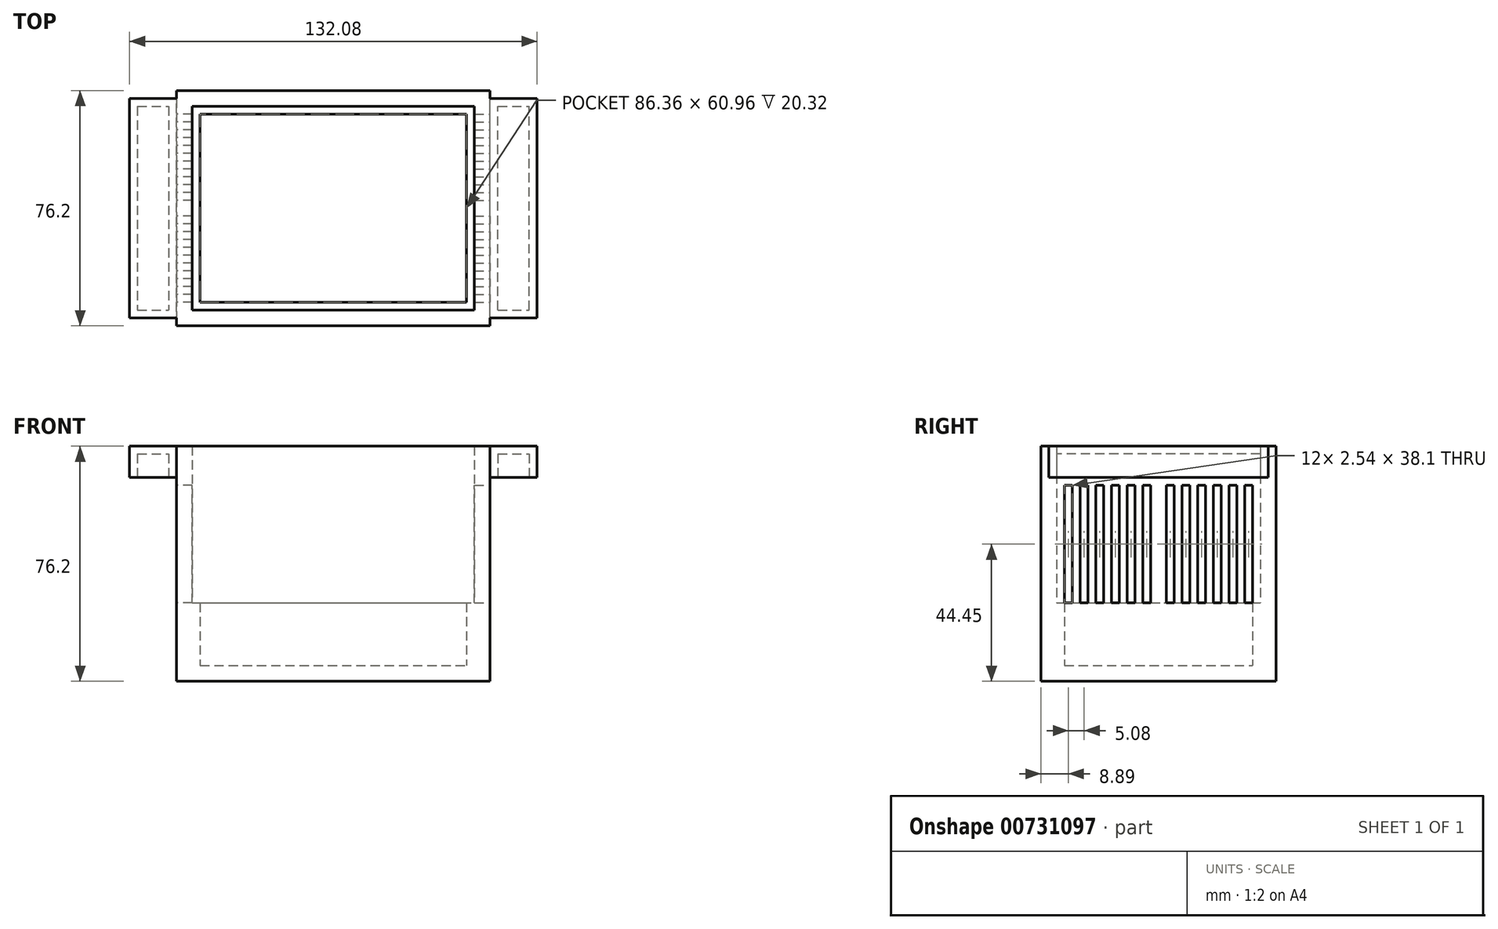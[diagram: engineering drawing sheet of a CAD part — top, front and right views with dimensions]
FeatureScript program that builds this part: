
annotation { "Feature Type Name" : "Feature", "Feature Type Description" : "" }
export const myFeature = defineFeature(function(context is Context, id is Id, definition is map)
    precondition{}
    {
        {
            var Q0;
            Q0=qCreatedBy(makeId("Top.planeOp"),FACE);
            var sketch = newSketch(context, id + "F0", { "sketchPlane" : qUnion([Q0])});
            skLineSegment(sketch, "E0.bottom", {"start": v(-50.8, -38.1) * mm, "end": v(50.8, -38.1) * mm});
            skLineSegment(sketch, "E0.top", {"start": v(-50.8, 38.1) * mm, "end": v(50.8, 38.1) * mm});
            skLineSegment(sketch, "E0.left", {"start": v(-50.8, -38.1) * mm, "end": v(-50.8, 38.1) * mm});
            skLineSegment(sketch, "E0.right", {"start": v(50.8, -38.1) * mm, "end": v(50.8, 38.1) * mm});
            skLineSegment(sketch, "E1.bottom", {"start": v(-45.72, -33.02) * mm, "end": v(45.72, -33.02) * mm});
            skLineSegment(sketch, "E1.top", {"start": v(-45.72, 33.02) * mm, "end": v(45.72, 33.02) * mm});
            skLineSegment(sketch, "E1.left", {"start": v(-45.72, -33.02) * mm, "end": v(-45.72, 33.02) * mm});
            skLineSegment(sketch, "E1.right", {"start": v(45.72, -33.02) * mm, "end": v(45.72, 33.02) * mm});
            skLineSegment(sketch, "E2.bottom", {"start": v(-43.18, -30.48) * mm, "end": v(43.18, -30.48) * mm});
            skLineSegment(sketch, "E2.top", {"start": v(-43.18, 30.48) * mm, "end": v(43.18, 30.48) * mm});
            skLineSegment(sketch, "E2.left", {"start": v(-43.18, -30.48) * mm, "end": v(-43.18, 30.48) * mm});
            skLineSegment(sketch, "E2.right", {"start": v(43.18, -30.48) * mm, "end": v(43.18, 30.48) * mm});
            skSolve(sketch);
        }
        {
            var Q0;
            Q0=makeQuery(id+"F0.imprint","IMPRINT",FACE,{"disambiguationData":[TD([[makeQuery(id+"F0.imprint","IMPRINT",EDGE,{"derivedFrom":sQuery(id+"F0.wireOp",EDGE,"E1.bottom")}),1.0]])]});
            extrude(context, id + "F1", {"entities" : qUnion([Q0]), "depth" : 25.4 * mm, "offsetDistance" : 25.4 * mm});
        }
        {
            var Q0;
            Q0 = qSketchRegion(id + "F0", true);
            extrude(context, id + "F2", {"entities" : qUnion([Q0]), "operationType" : NewBodyOperationType.ADD, "depth" : 76.2 * mm, "offsetDistance" : 25.4 * mm});
        }
        {
            var Q0;
            Q0=makeQuery(id+"F2.opExtrude","SWEPT_FACE",FACE,{"disambiguationData":[OSD([sQuery(id+"F0.wireOp",EDGE,"E0.left")])]});
            var sketch = newSketch(context, id + "F3", { "sketchPlane" : qUnion([Q0])});
            skLineSegment(sketch, "E3.bottom", {"start": v(-30.48, 25.4) * mm, "end": v(-27.94, 25.4) * mm});
            skLineSegment(sketch, "E3.top", {"start": v(-30.48, 63.5) * mm, "end": v(-27.94, 63.5) * mm});
            skLineSegment(sketch, "E3.left", {"start": v(-30.48, 25.4) * mm, "end": v(-30.48, 63.5) * mm});
            skLineSegment(sketch, "E3.right", {"start": v(-27.94, 25.4) * mm, "end": v(-27.94, 63.5) * mm});
            skLineSegment(sketch, "E4.bottom", {"start": v(-25.4, 25.4) * mm, "end": v(-22.86, 25.4) * mm});
            skLineSegment(sketch, "E4.top", {"start": v(-25.4, 63.5) * mm, "end": v(-22.86, 63.5) * mm});
            skLineSegment(sketch, "E4.left", {"start": v(-25.4, 25.4) * mm, "end": v(-25.4, 63.5) * mm});
            skLineSegment(sketch, "E4.right", {"start": v(-22.86, 25.4) * mm, "end": v(-22.86, 63.5) * mm});
            skLineSegment(sketch, "E5.bottom", {"start": v(-20.32, 25.4) * mm, "end": v(-17.78, 25.4) * mm});
            skLineSegment(sketch, "E5.top", {"start": v(-20.32, 63.5) * mm, "end": v(-17.78, 63.5) * mm});
            skLineSegment(sketch, "E5.left", {"start": v(-20.32, 25.4) * mm, "end": v(-20.32, 63.5) * mm});
            skLineSegment(sketch, "E5.right", {"start": v(-17.78, 25.4) * mm, "end": v(-17.78, 63.5) * mm});
            skLineSegment(sketch, "E6.bottom", {"start": v(-15.24, 25.4) * mm, "end": v(-12.7, 25.4) * mm});
            skLineSegment(sketch, "E6.top", {"start": v(-15.24, 63.5) * mm, "end": v(-12.7, 63.5) * mm});
            skLineSegment(sketch, "E6.left", {"start": v(-12.7, 25.4) * mm, "end": v(-12.7, 63.5) * mm});
            skLineSegment(sketch, "E6.right", {"start": v(-15.24, 25.4) * mm, "end": v(-15.24, 63.5) * mm});
            skLineSegment(sketch, "E7.bottom", {"start": v(-10.16, 25.4) * mm, "end": v(-7.62, 25.4) * mm});
            skLineSegment(sketch, "E7.top", {"start": v(-10.16, 63.5) * mm, "end": v(-7.62, 63.5) * mm});
            skLineSegment(sketch, "E7.left", {"start": v(-10.16, 25.4) * mm, "end": v(-10.16, 63.5) * mm});
            skLineSegment(sketch, "E7.right", {"start": v(-7.62, 25.4) * mm, "end": v(-7.62, 63.5) * mm});
            skLineSegment(sketch, "E8.bottom", {"start": v(-5.08, 25.4) * mm, "end": v(-2.54, 25.4) * mm});
            skLineSegment(sketch, "E8.top", {"start": v(-5.08, 63.5) * mm, "end": v(-2.54, 63.5) * mm});
            skLineSegment(sketch, "E8.left", {"start": v(-5.08, 25.4) * mm, "end": v(-5.08, 63.5) * mm});
            skLineSegment(sketch, "E8.right", {"start": v(-2.54, 25.4) * mm, "end": v(-2.54, 63.5) * mm});
            skLineSegment(sketch, "E9.bottom", {"start": v(2.54, 25.4) * mm, "end": v(5.08, 25.4) * mm});
            skLineSegment(sketch, "E9.top", {"start": v(2.54, 63.5) * mm, "end": v(5.08, 63.5) * mm});
            skLineSegment(sketch, "E9.left", {"start": v(2.54, 25.4) * mm, "end": v(2.54, 63.5) * mm});
            skLineSegment(sketch, "E9.right", {"start": v(5.08, 25.4) * mm, "end": v(5.08, 63.5) * mm});
            skLineSegment(sketch, "E10.bottom", {"start": v(7.62, 25.4) * mm, "end": v(10.16, 25.4) * mm});
            skLineSegment(sketch, "E10.top", {"start": v(7.62, 63.5) * mm, "end": v(10.16, 63.5) * mm});
            skLineSegment(sketch, "E10.left", {"start": v(7.62, 25.4) * mm, "end": v(7.62, 63.5) * mm});
            skLineSegment(sketch, "E10.right", {"start": v(10.16, 25.4) * mm, "end": v(10.16, 63.5) * mm});
            skLineSegment(sketch, "E11.bottom", {"start": v(12.7, 25.4) * mm, "end": v(15.24, 25.4) * mm});
            skLineSegment(sketch, "E11.top", {"start": v(12.7, 63.5) * mm, "end": v(15.24, 63.5) * mm});
            skLineSegment(sketch, "E11.left", {"start": v(12.7, 25.4) * mm, "end": v(12.7, 63.5) * mm});
            skLineSegment(sketch, "E11.right", {"start": v(15.24, 25.4) * mm, "end": v(15.24, 63.5) * mm});
            skLineSegment(sketch, "E12.bottom", {"start": v(17.78, 25.4) * mm, "end": v(20.32, 25.4) * mm});
            skLineSegment(sketch, "E12.top", {"start": v(17.78, 63.5) * mm, "end": v(20.32, 63.5) * mm});
            skLineSegment(sketch, "E12.left", {"start": v(17.78, 25.4) * mm, "end": v(17.78, 63.5) * mm});
            skLineSegment(sketch, "E12.right", {"start": v(20.32, 25.4) * mm, "end": v(20.32, 63.5) * mm});
            skLineSegment(sketch, "E13.bottom", {"start": v(22.86, 25.4) * mm, "end": v(25.4, 25.4) * mm});
            skLineSegment(sketch, "E13.top", {"start": v(22.86, 63.5) * mm, "end": v(25.4, 63.5) * mm});
            skLineSegment(sketch, "E13.left", {"start": v(22.86, 25.4) * mm, "end": v(22.86, 63.5) * mm});
            skLineSegment(sketch, "E13.right", {"start": v(25.4, 25.4) * mm, "end": v(25.4, 63.5) * mm});
            skLineSegment(sketch, "E14.bottom", {"start": v(27.94, 25.4) * mm, "end": v(30.48, 25.4) * mm});
            skLineSegment(sketch, "E14.top", {"start": v(27.94, 63.5) * mm, "end": v(30.48, 63.5) * mm});
            skLineSegment(sketch, "E14.left", {"start": v(27.94, 25.4) * mm, "end": v(27.94, 63.5) * mm});
            skLineSegment(sketch, "E14.right", {"start": v(30.48, 25.4) * mm, "end": v(30.48, 63.5) * mm});
            skSolve(sketch);
        }
        {
            var Q0;
            Q0 = qSketchRegion(id + "F3", true);
            extrude(context, id + "F4", {"entities" : qUnion([Q0]), "operationType" : NewBodyOperationType.REMOVE, "oppositeDirection" : true, "depth" : 5.08 * mm, "offsetDistance" : 25.4 * mm});
        }
        {
            var Q0;
            Q0=makeQuery(id+"F0.imprint","IMPRINT",FACE,{"disambiguationData":[TD([[makeQuery(id+"F0.imprint","IMPRINT",EDGE,{"derivedFrom":sQuery(id+"F0.wireOp",EDGE,"E2.bottom")}),1.0]])]});
            extrude(context, id + "F5", {"entities" : qUnion([Q0]), "operationType" : NewBodyOperationType.ADD, "depth" : 5.08 * mm, "offsetDistance" : 25.4 * mm});
        }
        {
            var Q0;
            Q0=makeQuery(id+"F2.opExtrude","SWEPT_FACE",FACE,{"disambiguationData":[OSD([sQuery(id+"F0.wireOp",EDGE,"E0.right")])]});
            var sketch = newSketch(context, id + "F6", { "sketchPlane" : qUnion([Q0])});
            skLineSegment(sketch, "E15.bottom", {"start": v(-2.54, 25.4) * mm, "end": v(-5.08, 25.4) * mm});
            skLineSegment(sketch, "E15.top", {"start": v(-2.54, 63.5) * mm, "end": v(-5.08, 63.5) * mm});
            skLineSegment(sketch, "E15.left", {"start": v(-2.54, 25.4) * mm, "end": v(-2.54, 63.5) * mm});
            skLineSegment(sketch, "E15.right", {"start": v(-5.08, 25.4) * mm, "end": v(-5.08, 63.5) * mm});
            skLineSegment(sketch, "E16.bottom", {"start": v(2.54, 25.4) * mm, "end": v(5.08, 25.4) * mm});
            skLineSegment(sketch, "E16.top", {"start": v(2.54, 63.5) * mm, "end": v(5.08, 63.5) * mm});
            skLineSegment(sketch, "E16.left", {"start": v(2.54, 25.4) * mm, "end": v(2.54, 63.5) * mm});
            skLineSegment(sketch, "E16.right", {"start": v(5.08, 25.4) * mm, "end": v(5.08, 63.5) * mm});
            skLineSegment(sketch, "E17.bottom", {"start": v(7.62, 25.4) * mm, "end": v(10.16, 25.4) * mm});
            skLineSegment(sketch, "E17.top", {"start": v(7.62, 63.5) * mm, "end": v(10.16, 63.5) * mm});
            skLineSegment(sketch, "E17.left", {"start": v(7.62, 25.4) * mm, "end": v(7.62, 63.5) * mm});
            skLineSegment(sketch, "E17.right", {"start": v(10.16, 25.4) * mm, "end": v(10.16, 63.5) * mm});
            skLineSegment(sketch, "E18.bottom", {"start": v(12.7, 25.4) * mm, "end": v(15.24, 25.4) * mm});
            skLineSegment(sketch, "E18.top", {"start": v(12.7, 63.5) * mm, "end": v(15.24, 63.5) * mm});
            skLineSegment(sketch, "E18.left", {"start": v(12.7, 25.4) * mm, "end": v(12.7, 63.5) * mm});
            skLineSegment(sketch, "E18.right", {"start": v(15.24, 25.4) * mm, "end": v(15.24, 63.5) * mm});
            skLineSegment(sketch, "E19.bottom", {"start": v(-7.62, 25.4) * mm, "end": v(-10.16, 25.4) * mm});
            skLineSegment(sketch, "E19.top", {"start": v(-7.62, 63.5) * mm, "end": v(-10.16, 63.5) * mm});
            skLineSegment(sketch, "E19.left", {"start": v(-7.62, 25.4) * mm, "end": v(-7.62, 63.5) * mm});
            skLineSegment(sketch, "E19.right", {"start": v(-10.16, 25.4) * mm, "end": v(-10.16, 63.5) * mm});
            skLineSegment(sketch, "E20.bottom", {"start": v(-12.7, 25.4) * mm, "end": v(-15.24, 25.4) * mm});
            skLineSegment(sketch, "E20.top", {"start": v(-12.7, 63.5) * mm, "end": v(-15.24, 63.5) * mm});
            skLineSegment(sketch, "E20.left", {"start": v(-12.7, 25.4) * mm, "end": v(-12.7, 63.5) * mm});
            skLineSegment(sketch, "E20.right", {"start": v(-15.24, 25.4) * mm, "end": v(-15.24, 63.5) * mm});
            skLineSegment(sketch, "E21.bottom", {"start": v(17.78, 25.4) * mm, "end": v(20.32, 25.4) * mm});
            skLineSegment(sketch, "E21.top", {"start": v(17.78, 63.5) * mm, "end": v(20.32, 63.5) * mm});
            skLineSegment(sketch, "E21.left", {"start": v(17.78, 25.4) * mm, "end": v(17.78, 63.5) * mm});
            skLineSegment(sketch, "E21.right", {"start": v(20.32, 25.4) * mm, "end": v(20.32, 63.5) * mm});
            skLineSegment(sketch, "E22.bottom", {"start": v(22.86, 25.4) * mm, "end": v(25.4, 25.4) * mm});
            skLineSegment(sketch, "E22.top", {"start": v(22.86, 63.5) * mm, "end": v(25.4, 63.5) * mm});
            skLineSegment(sketch, "E22.left", {"start": v(22.86, 25.4) * mm, "end": v(22.86, 63.5) * mm});
            skLineSegment(sketch, "E22.right", {"start": v(25.4, 25.4) * mm, "end": v(25.4, 63.5) * mm});
            skLineSegment(sketch, "E23.bottom", {"start": v(27.94, 25.4) * mm, "end": v(30.48, 25.4) * mm});
            skLineSegment(sketch, "E23.top", {"start": v(27.94, 63.5) * mm, "end": v(30.48, 63.5) * mm});
            skLineSegment(sketch, "E23.left", {"start": v(27.94, 25.4) * mm, "end": v(27.94, 63.5) * mm});
            skLineSegment(sketch, "E23.right", {"start": v(30.48, 25.4) * mm, "end": v(30.48, 63.5) * mm});
            skLineSegment(sketch, "E24.bottom", {"start": v(-17.78, 25.4) * mm, "end": v(-20.32, 25.4) * mm});
            skLineSegment(sketch, "E24.top", {"start": v(-17.78, 63.5) * mm, "end": v(-20.32, 63.5) * mm});
            skLineSegment(sketch, "E24.left", {"start": v(-17.78, 25.4) * mm, "end": v(-17.78, 63.5) * mm});
            skLineSegment(sketch, "E24.right", {"start": v(-20.32, 25.4) * mm, "end": v(-20.32, 63.5) * mm});
            skLineSegment(sketch, "E25.bottom", {"start": v(-22.86, 25.4) * mm, "end": v(-25.4, 25.4) * mm});
            skLineSegment(sketch, "E25.top", {"start": v(-22.86, 63.5) * mm, "end": v(-25.4, 63.5) * mm});
            skLineSegment(sketch, "E25.left", {"start": v(-22.86, 25.4) * mm, "end": v(-22.86, 63.5) * mm});
            skLineSegment(sketch, "E25.right", {"start": v(-25.4, 25.4) * mm, "end": v(-25.4, 63.5) * mm});
            skLineSegment(sketch, "E26.bottom", {"start": v(-27.94, 25.4) * mm, "end": v(-30.48, 25.4) * mm});
            skLineSegment(sketch, "E26.top", {"start": v(-27.94, 63.5) * mm, "end": v(-30.48, 63.5) * mm});
            skLineSegment(sketch, "E26.left", {"start": v(-27.94, 25.4) * mm, "end": v(-27.94, 63.5) * mm});
            skLineSegment(sketch, "E26.right", {"start": v(-30.48, 25.4) * mm, "end": v(-30.48, 63.5) * mm});
            skSolve(sketch);
        }
        {
            var Q0;
            Q0 = qSketchRegion(id + "F6", true);
            extrude(context, id + "F7", {"entities" : qUnion([Q0]), "operationType" : NewBodyOperationType.REMOVE, "oppositeDirection" : true, "depth" : 5.08 * mm, "offsetDistance" : 25.4 * mm});
        }
        {
            var Q0;
            Q0=makeQuery(id+"F2.opExtrude","SWEPT_FACE",FACE,{"disambiguationData":[OSD([sQuery(id+"F0.wireOp",EDGE,"E0.right")])]});
            var sketch = newSketch(context, id + "F8", { "sketchPlane" : qUnion([Q0])});
            skLineSegment(sketch, "E27.bottom", {"start": v(-35.56, 76.2) * mm, "end": v(35.56, 76.2) * mm});
            skLineSegment(sketch, "E27.top", {"start": v(-35.56, 66.04) * mm, "end": v(35.56, 66.04) * mm});
            skLineSegment(sketch, "E27.left", {"start": v(-35.56, 76.2) * mm, "end": v(-35.56, 66.04) * mm});
            skLineSegment(sketch, "E27.right", {"start": v(35.56, 76.2) * mm, "end": v(35.56, 66.04) * mm});
            skSolve(sketch);
        }
        {
            var Q0;
            Q0 = qSketchRegion(id + "F8", true);
            extrude(context, id + "F9", {"entities" : qUnion([Q0]), "operationType" : NewBodyOperationType.ADD, "depth" : 15.24 * mm, "offsetDistance" : 25.4 * mm});
        }
        {
            var Q0;
            Q0=makeQuery(id+"F2.opExtrude","SWEPT_FACE",FACE,{"disambiguationData":[OSD([sQuery(id+"F0.wireOp",EDGE,"E0.left")])]});
            var sketch = newSketch(context, id + "F10", { "sketchPlane" : qUnion([Q0])});
            skLineSegment(sketch, "E28.bottom", {"start": v(-35.56, 76.2) * mm, "end": v(35.56, 76.2) * mm});
            skLineSegment(sketch, "E28.top", {"start": v(-35.56, 66.04) * mm, "end": v(35.56, 66.04) * mm});
            skLineSegment(sketch, "E28.left", {"start": v(-35.56, 76.2) * mm, "end": v(-35.56, 66.04) * mm});
            skLineSegment(sketch, "E28.right", {"start": v(35.56, 76.2) * mm, "end": v(35.56, 66.04) * mm});
            skSolve(sketch);
        }
        {
            var Q0;
            Q0 = qSketchRegion(id + "F10", true);
            extrude(context, id + "F11", {"entities" : qUnion([Q0]), "operationType" : NewBodyOperationType.ADD, "depth" : 15.24 * mm, "offsetDistance" : 25.4 * mm});
        }
        {
            var Q0;
            Q0=makeQuery(id+"F9.opExtrude","SWEPT_FACE",FACE,{"disambiguationData":[OSD([sQuery(id+"F8.wireOp",EDGE,"E27.top")])]});
            var sketch = newSketch(context, id + "F12", { "sketchPlane" : qUnion([Q0])});
            skLineSegment(sketch, "E29.bottom", {"start": v(53.34, 33.02) * mm, "end": v(63.5, 33.02) * mm});
            skLineSegment(sketch, "E29.top", {"start": v(53.34, -33.02) * mm, "end": v(63.5, -33.02) * mm});
            skLineSegment(sketch, "E29.left", {"start": v(53.34, 33.02) * mm, "end": v(53.34, -33.02) * mm});
            skLineSegment(sketch, "E29.right", {"start": v(63.5, 33.02) * mm, "end": v(63.5, -33.02) * mm});
            skLineSegment(sketch, "E30.bottom", {"start": v(-63.5, -33.02) * mm, "end": v(-53.34, -33.02) * mm});
            skLineSegment(sketch, "E30.top", {"start": v(-63.5, 33.02) * mm, "end": v(-53.34, 33.02) * mm});
            skLineSegment(sketch, "E30.left", {"start": v(-63.5, -33.02) * mm, "end": v(-63.5, 33.02) * mm});
            skLineSegment(sketch, "E30.right", {"start": v(-53.34, -33.02) * mm, "end": v(-53.34, 33.02) * mm});
            skSolve(sketch);
        }
        {
            var Q0;
            Q0 = qSketchRegion(id + "F12", true);
            extrude(context, id + "F13", {"entities" : qUnion([Q0]), "operationType" : NewBodyOperationType.REMOVE, "oppositeDirection" : true, "depth" : 7.62 * mm, "offsetDistance" : 25.4 * mm});
        }
    });
